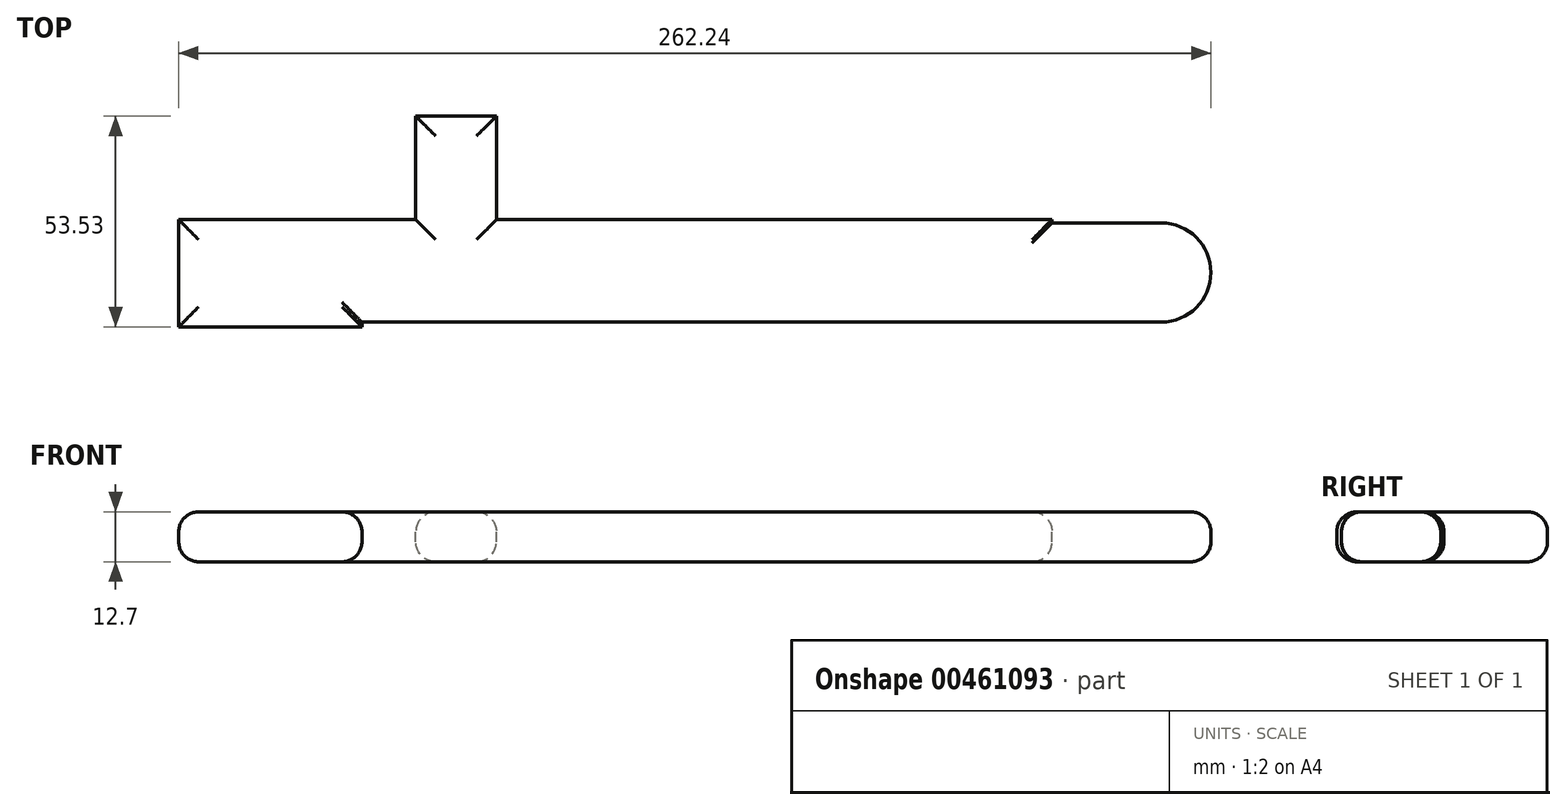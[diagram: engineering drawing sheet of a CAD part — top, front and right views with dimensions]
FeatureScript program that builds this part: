
annotation { "Feature Type Name" : "Feature", "Feature Type Description" : "" }
export const myFeature = defineFeature(function(context is Context, id is Id, definition is map)
    precondition{}
    {
        {
            var Q0;
            Q0=qCreatedBy(makeId("Top.planeOp"),FACE);
            var sketch = newSketch(context, id + "F0", { "sketchPlane" : qUnion([Q0])});
            skLineSegment(sketch, "E0.bottom", {"start": v(-25.83, 9.25) * mm, "end": v(161.65, 9.25) * mm});
            skLineSegment(sketch, "E0.top", {"start": v(-25.83, -16.79) * mm, "end": v(161.65, -16.79) * mm});
            skLineSegment(sketch, "E0.left", {"start": v(-25.83, 9.25) * mm, "end": v(-25.83, -16.79) * mm});
            skLineSegment(sketch, "E0.right", {"start": v(161.65, 9.25) * mm, "end": v(161.65, -16.79) * mm});
            skLineSegment(sketch, "E1.bottom", {"start": v(0, -16.79) * mm, "end": v(20.5, -16.79) * mm});
            skLineSegment(sketch, "E1.top", {"start": v(0, -43.1) * mm, "end": v(20.5, -43.1) * mm});
            skLineSegment(sketch, "E1.left", {"start": v(0, -16.79) * mm, "end": v(0, -43.1) * mm});
            skLineSegment(sketch, "E1.right", {"start": v(20.5, -16.79) * mm, "end": v(20.5, -43.1) * mm});
            skPoint(sketch, "E2.endSnap0", {"position": v(10.25, -43.1) * mm});
            skLineSegment(sketch, "E3.MirrorCS", {"start": v(20.5, 9.25) * mm, "end": v(20.5, 35.56) * mm});
            skLineSegment(sketch, "E4.MirrorCS", {"start": v(0, 35.56) * mm, "end": v(20.5, 35.56) * mm});
            skLineSegment(sketch, "E5.MirrorCS", {"start": v(0, 9.25) * mm, "end": v(0, 35.56) * mm});
            skLineSegment(sketch, "E6.MirrorCS", {"start": v(0, 9.25) * mm, "end": v(20.5, 9.25) * mm});
            skLineSegment(sketch, "E7.bottom", {"start": v(-13.68, 9.25) * mm, "end": v(-60.24, 9.25) * mm});
            skLineSegment(sketch, "E7.top", {"start": v(-13.68, -17.97) * mm, "end": v(-60.24, -17.97) * mm});
            skLineSegment(sketch, "E7.left", {"start": v(-13.68, 9.25) * mm, "end": v(-13.68, -17.97) * mm});
            skLineSegment(sketch, "E7.right", {"start": v(-60.24, 9.25) * mm, "end": v(-60.24, -17.97) * mm});
            skLineSegment(sketch, "E8.bottom", {"start": v(161.65, -16.79) * mm, "end": v(189.4, -16.79) * mm});
            skLineSegment(sketch, "E8.top", {"start": v(161.65, 8.43) * mm, "end": v(189.4, 8.43) * mm});
            skLineSegment(sketch, "E8.left", {"start": v(161.65, -16.79) * mm, "end": v(161.65, 8.43) * mm});
            skLineSegment(sketch, "E8.right", {"start": v(189.4, -16.79) * mm, "end": v(189.4, 8.43) * mm});
            skArc(sketch, "E9", {"start": v(189.4, -16.79) * mm, "mid": v(198.29, -13.11) * mm, "end": v(202, -4.23) * mm});
            skArc(sketch, "E10", {"start": v(202, -4.23) * mm, "mid": v(198.33, 4.72) * mm, "end": v(189.4, 8.43) * mm});
            skSolve(sketch);
        }
        {
            var Q0;
            {var subQ1=sQuery(id+"F0.wireOp",EDGE,"E0.left");Q0=makeQuery(id+"F0.imprint","IMPRINT",FACE,{"disambiguationData":[TD([[makeQuery(id+"F0.imprint","IMPRINT",EDGE,{"derivedFrom":subQ1}),-1.0]])]});}
            var Q1;
            Q1=makeQuery(id+"F0.imprint","IMPRINT",FACE,{"disambiguationData":[TD([[makeQuery(id+"F0.imprint","IMPRINT",EDGE,{"derivedFrom":sQuery(id+"F0.wireOp",EDGE,"E1.bottom")}),-1.0]])]});
            var Q2;
            Q2=makeQuery(id+"F0.imprint","IMPRINT",FACE,{"disambiguationData":[TD([[makeQuery(id+"F0.imprint","IMPRINT",EDGE,{"derivedFrom":sQuery(id+"F0.wireOp",EDGE,"E3.MirrorCS")}),1.0]])]});
            var Q3;
            Q3=makeQuery(id+"F0.imprint","IMPRINT",FACE,{"disambiguationData":[TD([[makeQuery(id+"F0.imprint","IMPRINT",EDGE,{"derivedFrom":sQuery(id+"F0.wireOp",EDGE,"E8.right")}),-1.0]])]});
            var Q4;
            {var subQ0=sQuery(id+"F0.wireOp",EDGE,"E0.left");Q4=makeQuery(id+"F0.imprint","IMPRINT",FACE,{"disambiguationData":[TD([[makeQuery(id+"F0.imprint","IMPRINT",EDGE,{"derivedFrom":subQ0}),1.0]])]});}
            var Q5;
            Q5=makeQuery(id+"F0.imprint","IMPRINT",FACE,{"disambiguationData":[TD([[makeQuery(id+"F0.imprint","IMPRINT",EDGE,{"derivedFrom":sQuery(id+"F0.wireOp",EDGE,"E8.bottom")}),1.0]])]});
            var Q6;
            {var subQ6=sQuery(id+"F0.wireOp",EDGE,"E0.right");Q6=makeQuery(id+"F0.imprint","IMPRINT",FACE,{"disambiguationData":[TD([[makeQuery(id+"F0.imprint","IMPRINT",EDGE,{"derivedFrom":subQ6}),-1.0]])]});}
            extrude(context, id + "F1", {"entities" : qUnion([Q0, Q1, Q2, Q3, Q4, Q5, Q6]), "oppositeDirection" : true, "depth" : 12.7 * mm});
        }
        {
            var Q0;
            Q0=makeQuery(id+"F1.opExtrude","CAP_EDGE",EDGE,{"disambiguationData":[OSD([sQuery(id+"F0.wireOp",EDGE,"E7.top")])],"isStart":true});
            var Q1;
            Q1=makeQuery(id+"F1.opExtrude","CAP_FACE",FACE,{"disambiguationData":[OSD([sQuery(id+"F0.wireOp",EDGE,"E0.bottom"),sQuery(id+"F0.wireOp",EDGE,"E0.top"),sQuery(id+"F0.wireOp",EDGE,"E0.right"),sQuery(id+"F0.wireOp",EDGE,"E1.top"),sQuery(id+"F0.wireOp",EDGE,"E1.left"),sQuery(id+"F0.wireOp",EDGE,"E1.right"),sQuery(id+"F0.wireOp",EDGE,"E3.MirrorCS"),sQuery(id+"F0.wireOp",EDGE,"E4.MirrorCS"),sQuery(id+"F0.wireOp",EDGE,"E5.MirrorCS"),sQuery(id+"F0.wireOp",EDGE,"E7.bottom"),sQuery(id+"F0.wireOp",EDGE,"E7.top"),sQuery(id+"F0.wireOp",EDGE,"E7.left"),sQuery(id+"F0.wireOp",EDGE,"E7.right"),sQuery(id+"F0.wireOp",EDGE,"E8.bottom"),sQuery(id+"F0.wireOp",EDGE,"E8.top"),sQuery(id+"F0.wireOp",EDGE,"E9"),sQuery(id+"F0.wireOp",EDGE,"E10")])],"isStart":true});
            var Q2;
            Q2=makeQuery(id+"F1.opExtrude","CAP_FACE",FACE,{"disambiguationData":[OSD([sQuery(id+"F0.wireOp",EDGE,"E0.bottom"),sQuery(id+"F0.wireOp",EDGE,"E0.top"),sQuery(id+"F0.wireOp",EDGE,"E0.right"),sQuery(id+"F0.wireOp",EDGE,"E1.top"),sQuery(id+"F0.wireOp",EDGE,"E1.left"),sQuery(id+"F0.wireOp",EDGE,"E1.right"),sQuery(id+"F0.wireOp",EDGE,"E3.MirrorCS"),sQuery(id+"F0.wireOp",EDGE,"E4.MirrorCS"),sQuery(id+"F0.wireOp",EDGE,"E5.MirrorCS"),sQuery(id+"F0.wireOp",EDGE,"E7.bottom"),sQuery(id+"F0.wireOp",EDGE,"E7.top"),sQuery(id+"F0.wireOp",EDGE,"E7.left"),sQuery(id+"F0.wireOp",EDGE,"E7.right"),sQuery(id+"F0.wireOp",EDGE,"E8.bottom"),sQuery(id+"F0.wireOp",EDGE,"E8.top"),sQuery(id+"F0.wireOp",EDGE,"E9"),sQuery(id+"F0.wireOp",EDGE,"E10")])],"isStart":false});
            fillet(context, id + "F2", {"entities" : qUnion([Q0, Q1, Q2]), "radius" : 5.08 * mm, "tangentPropagation" : true, "allowEdgeOverflow" : false});
        }
    });
